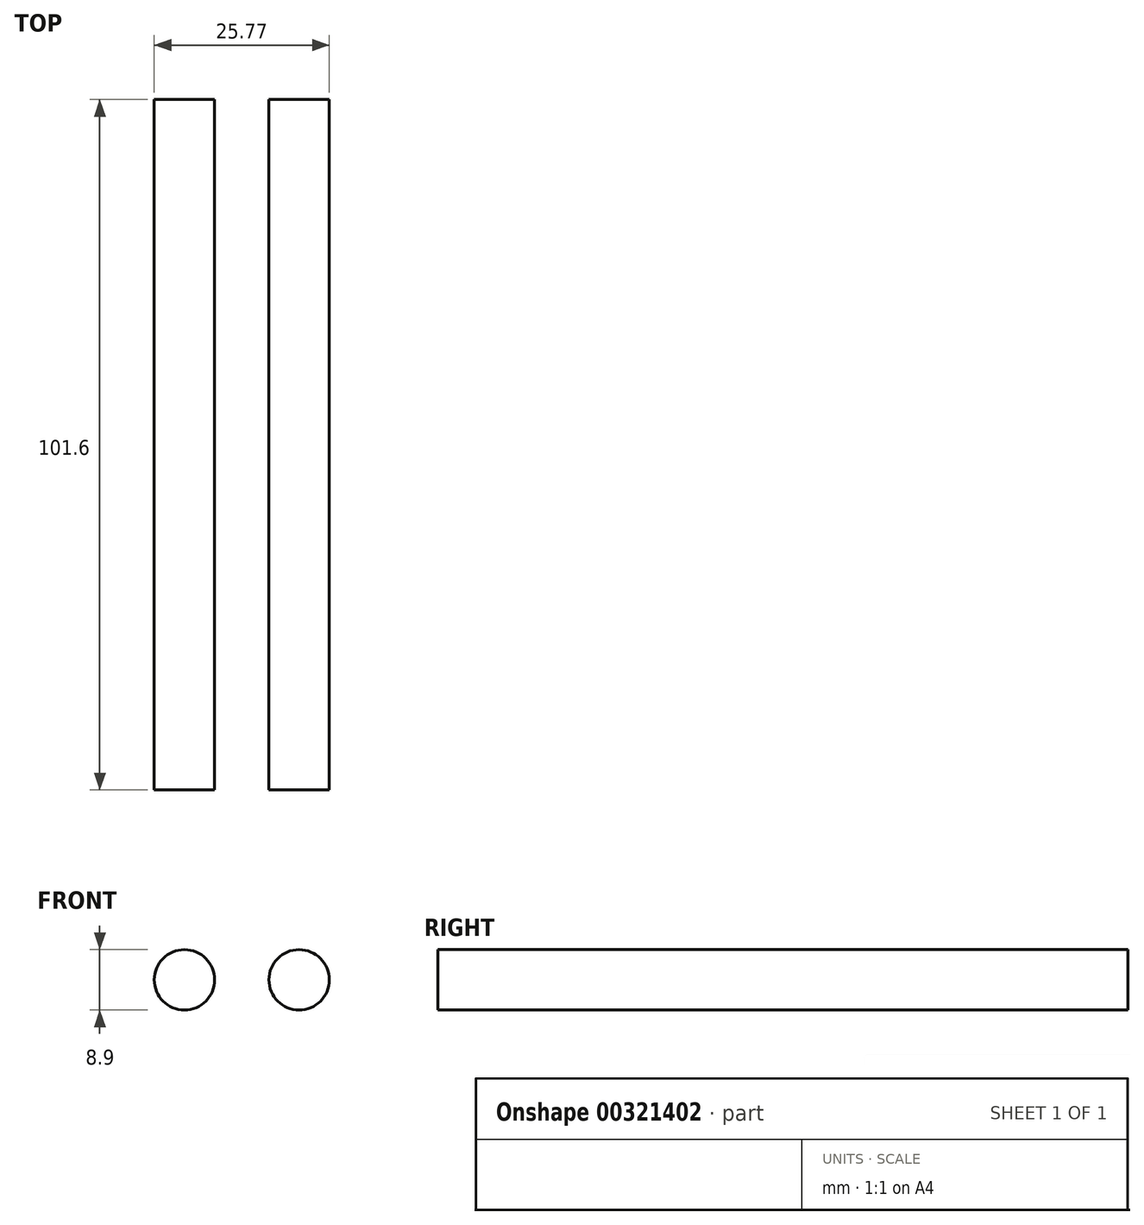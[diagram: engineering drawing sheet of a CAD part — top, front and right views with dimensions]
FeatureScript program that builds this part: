
annotation { "Feature Type Name" : "Feature", "Feature Type Description" : "" }
export const myFeature = defineFeature(function(context is Context, id is Id, definition is map)
    precondition{}
    {
        {
            var Q0;
            Q0=qCreatedBy(makeId("Front.planeOp"),FACE);
            var sketch = newSketch(context, id + "F0", { "sketchPlane" : qUnion([Q0])});
            skCircle(sketch, "E0", {"center": v(0, 0) * mm, "radius": 4.45 * mm});
            skCircle(sketch, "E1", {"center": v(16.87, 0) * mm, "radius": 4.45 * mm});
            skSolve(sketch);
        }
        {
            var Q0;
            Q0 = qSketchRegion(id + "F0", true);
            extrude(context, id + "F1", {"entities" : qUnion([Q0]), "depth" : 101.6 * mm});
        }
    });
